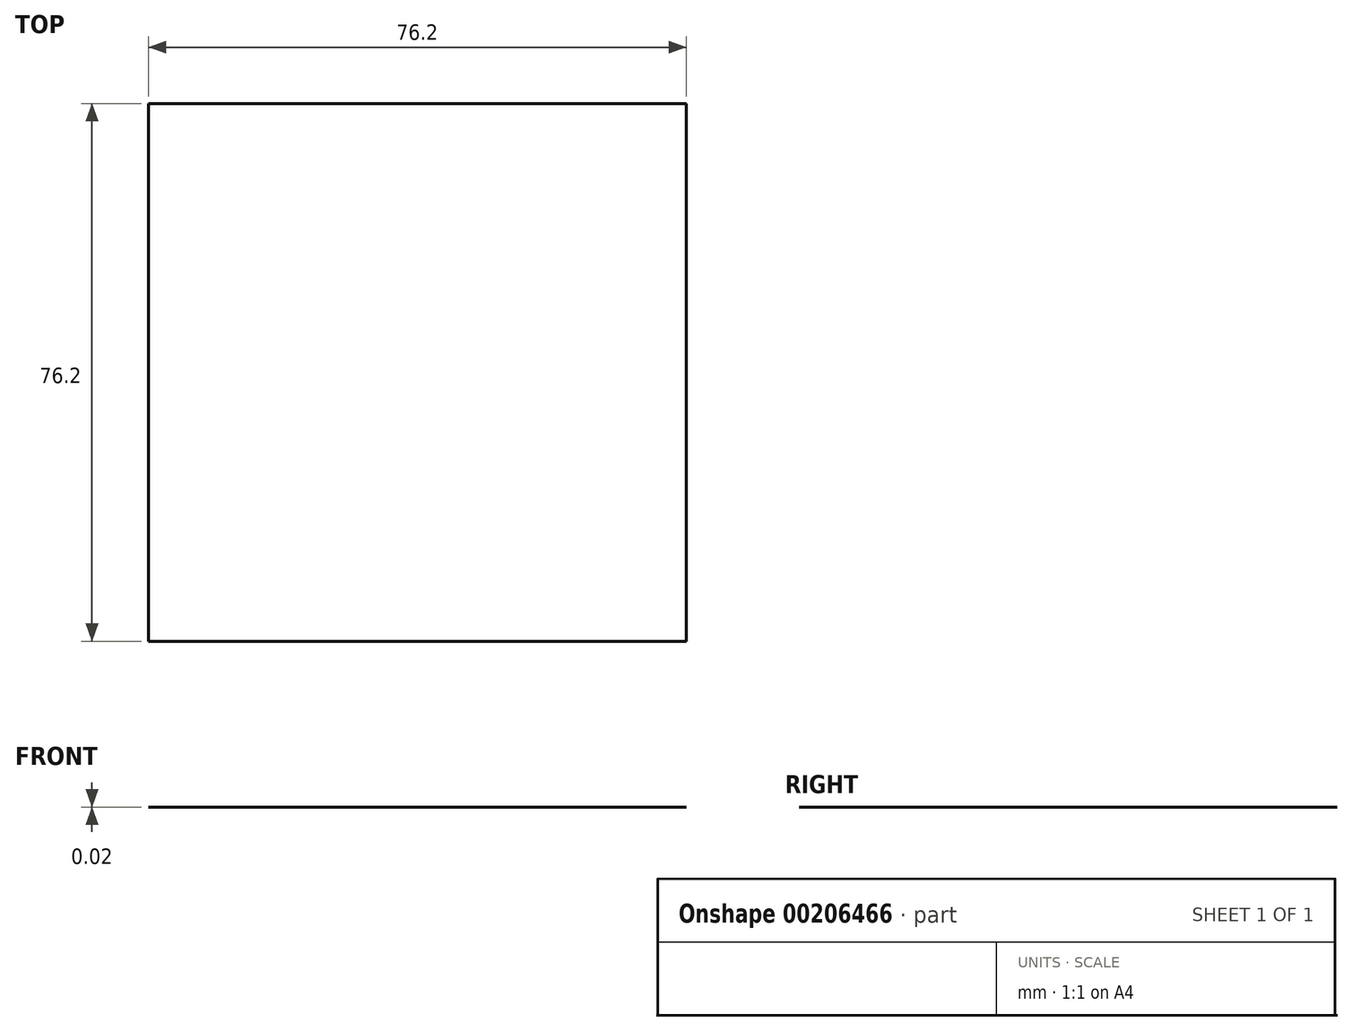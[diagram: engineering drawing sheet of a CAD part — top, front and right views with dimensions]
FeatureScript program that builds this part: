
annotation { "Feature Type Name" : "Feature", "Feature Type Description" : "" }
export const myFeature = defineFeature(function(context is Context, id is Id, definition is map)
    precondition{}
    {
        {
            var Q0;
            Q0=qCreatedBy(makeId("Top.planeOp"),FACE);
            var sketch = newSketch(context, id + "F0", { "sketchPlane" : qUnion([Q0])});
            skLineSegment(sketch, "E0.bottom", {"start": v(38.1, 38.1) * mm, "end": v(-38.1, 38.1) * mm});
            skLineSegment(sketch, "E0.top", {"start": v(38.1, -38.1) * mm, "end": v(-38.1, -38.1) * mm});
            skLineSegment(sketch, "E0.left", {"start": v(38.1, 38.1) * mm, "end": v(38.1, -38.1) * mm});
            skLineSegment(sketch, "E0.right", {"start": v(-38.1, 38.1) * mm, "end": v(-38.1, -38.1) * mm});
            skPoint(sketch, "E0.middle", {"position": v(0, 0) * mm});
            skLineSegment(sketch, "E1.0", {"start": v(25.4, 25.4) * mm, "end": v(25.4, -25.4) * mm});
            skLineSegment(sketch, "E1.1", {"start": v(25.4, 25.4) * mm, "end": v(-25.4, 25.4) * mm});
            skLineSegment(sketch, "E1.2", {"start": v(-25.4, 25.4) * mm, "end": v(-25.4, -25.4) * mm});
            skLineSegment(sketch, "E1.3", {"start": v(25.4, -25.4) * mm, "end": v(-25.4, -25.4) * mm});
            skSolve(sketch);
        }
        {
            var Q0;
            Q0 = qSketchRegion(id + "F0", true);
            var Q1;
            Q1=makeQuery(id+"F0.imprint","IMPRINT",FACE,{"disambiguationData":[TD([[makeQuery(id+"F0.imprint","IMPRINT",EDGE,{"derivedFrom":sQuery(id+"F0.wireOp",EDGE,"E1.0")}),-1.0]])]});
            extrude(context, id + "F1", {"entities" : qUnion([Q0, Q1]), "endBound" : BoundingType.SYMMETRIC, "depth" : 9 / 406.4 * mm});
        }
    });
